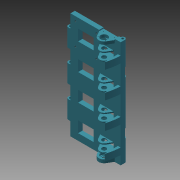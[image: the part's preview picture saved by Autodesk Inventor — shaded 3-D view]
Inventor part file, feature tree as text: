
AUTODESK INVENTOR PART (.ipt)
format: ipt  version: 2015 (Build 190159000, 159)  size: 471,040 bytes
history: native  units: mm
features: extrude x20, sketch x20, thread x8, pattern_linear x4, plane x1, projected_geometry x1
ambient origin geometry x8: Origin, YZ Plane, XZ Plane, XY Plane, X Axis, Y Axis, Z Axis, Center Point
bodies: 实体1 (feature_tree)
feature tree (54):
  extrude  "拉伸1"  Depth=20.0mm
  extrude  "拉伸2"  Depth=2.0mm
  extrude  "拉伸3"  Depth=20.0mm
  extrude  "拉伸4"  Depth=48.0mm
  extrude  "拉伸5"  Depth=175.0mm
  extrude  "拉伸6"  Depth=15.0mm TaperAngle=0.0deg
  extrude  "拉伸7"  Depth=18.0mm TaperAngle=0.0deg
  extrude  "拉伸8"  Depth=2.0mm TaperAngle=0.0deg
  extrude  "拉伸9"  Depth=2.0mm TaperAngle=0.0deg
  extrude  "拉伸10"  Depth=90.0mm
  pattern_linear  "矩形阵列1"  Count1=3  [1 undecoded]
  extrude  "拉伸11"  Depth=30.0mm
  extrude  "拉伸12"  Depth=90.0mm
  extrude  "拉伸13"  Depth=40.0mm
  pattern_linear  "矩形阵列2"  Count1=42 Spacing1=0.0mm
  extrude  "拉伸14"  Depth=5.0mm
  extrude  "拉伸15"  Depth=5.0mm
  thread  "螺纹1"  [1 undecoded]
  thread  "螺纹2"  [1 undecoded]
  thread  "螺纹3"  [1 undecoded]
  thread  "螺纹4"  [1 undecoded]
  extrude  "拉伸16"  Depth=5.0mm
  extrude  "拉伸17"  Depth=5.0mm
  thread  "螺纹5"  [1 undecoded]
  thread  "螺纹6"  [1 undecoded]
  thread  "螺纹7"  [1 undecoded]
  thread  "螺纹8"  [1 undecoded]
  extrude  "拉伸18"  Depth=20.0mm
  pattern_linear  "矩形阵列3"  Count1=42 Spacing1=0.0mm
  extrude  "拉伸19"  Depth=20.0mm
  plane  "工作平面1"
  extrude  "拉伸20"  TaperAngle=30.0deg  [1 undecoded]
  pattern_linear  "矩形阵列4"  Spacing1=5.0mm  [1 undecoded]
  sketch  "草图1"  dims[d0=227.0mm d1=20.0mm]
  sketch  "草图2"  dims[d2=10.0mm d3=2.0mm]
  sketch  "草图3"  dims[d4=60.0mm d5=20.0mm]
  sketch  "草图4"  dims[d6=483.0mm d7=0.0mm d8=48.0mm]
  sketch  "草图5"  dims[d9=120.0deg d10=175.0mm]
  sketch  "草图6"  dims[d11=22.5mm d12=15.0mm d13=0.0mm]
  sketch  "草图7"  dims[d14=32.0mm d15=18.0mm d16=0.0mm]
  sketch  "草图8"  dims[d17=24.0mm d18=2.0mm d19=0.0mm]
  projected_geometry  "投影回路1"
  sketch  "草图10"  dims[d20=15.0mm d21=2.0mm d22=0.0mm]
  sketch  "草图11"  dims[d23=40.0mm d24=90.0mm d25=30.0mm]
  sketch  "草图12"  dims[d26=90.0mm d27=30.0mm]
  sketch  "草图13"  dims[d28=30.0mm d29=90.0mm]
  sketch  "草图14"  dims[d31=2.0mm d32=0.0mm d33=40.0mm d35=420.0mm d36=0.0mm]
  sketch  "草图15"  dims[d37=20.0mm d38=5.0mm]
  sketch  "草图16"  dims[d39=30.0mm d40=5.0mm d41=80.0mm d42=5.0mm d43=30.0mm d44=5.0mm]
  sketch  "草图17"  dims[d45=80.0mm d46=5.0mm]
  sketch  "草图18"  dims[d47=30.0mm d48=5.0mm d49=80.0mm d50=5.0mm d51=30.0mm d52=5.0mm]
  sketch  "草图19"  dims[d53=420.0mm d54=0.0mm d55=20.0mm d56=420.0mm d57=0.0mm]
  sketch  "草图20"  dims[d58=20.0mm d59=1.6mm]
  sketch  "草图21"  dims[d60=6.0mm d61=30.0deg d62=5.0mm d63=0.0mm d64=40.0mm d66=120.0mm d67=48.0mm d68=18.0mm d69=0.0mm d70=32.0mm d71=18.0mm d72=0.0mm d73=20.0mm d74=0.0mm d75=40.0mm d77=120.0mm d78=53.0mm d79=30.0mm d80=48.0mm d81=5.0mm d82=0.0mm d83=3.0mm d84=3.0mm d85=3.0mm d86=3.0mm d87=20.0mm d88=10.0mm d89=10.0mm d90=10.0mm d91=10.0mm d92=10.0mm d93=10.0mm d94=13.0mm d95=0.0mm d96=10.0mm d97=0.0mm d98=10.0mm d99=0.0mm d100=10.0mm d101=0.0mm d102=10.0mm d103=0.0mm d104=60.0mm d105=20.0mm d106=81.0mm d107=81.0mm d108=81.0mm d109=10.0mm d110=0.0mm d111=8.0mm d112=8.0mm d113=8.0mm d114=8.0mm d115=20.0mm d116=20.0mm d117=120.0mm d118=120.0mm d119=32.5mm d120=32.5mm d121=95.0mm d122=95.0mm d123=20.0mm d124=0.0mm d125=10.0mm d126=0.0mm d127=10.0mm d128=0.0mm d129=10.0mm d130=0.0mm d131=10.0mm d132=0.0mm d133=70.0mm d134=10.0mm d135=10.0mm d136=30.0mm d137=10.0mm d138=0.0mm d139=40.0mm d141=120.0mm d142=10.0mm d143=10.0mm d144=0.0mm d145=-108.0mm d146=20.0mm d147=40.0mm d148=0.0mm d149=20.0mm d151=240.0mm]
note: 11 required parameter values undecoded (feature->parameter linkage not recoverable at this tier; creation-order binding heuristic only, values carry confidence <= 0.55)
